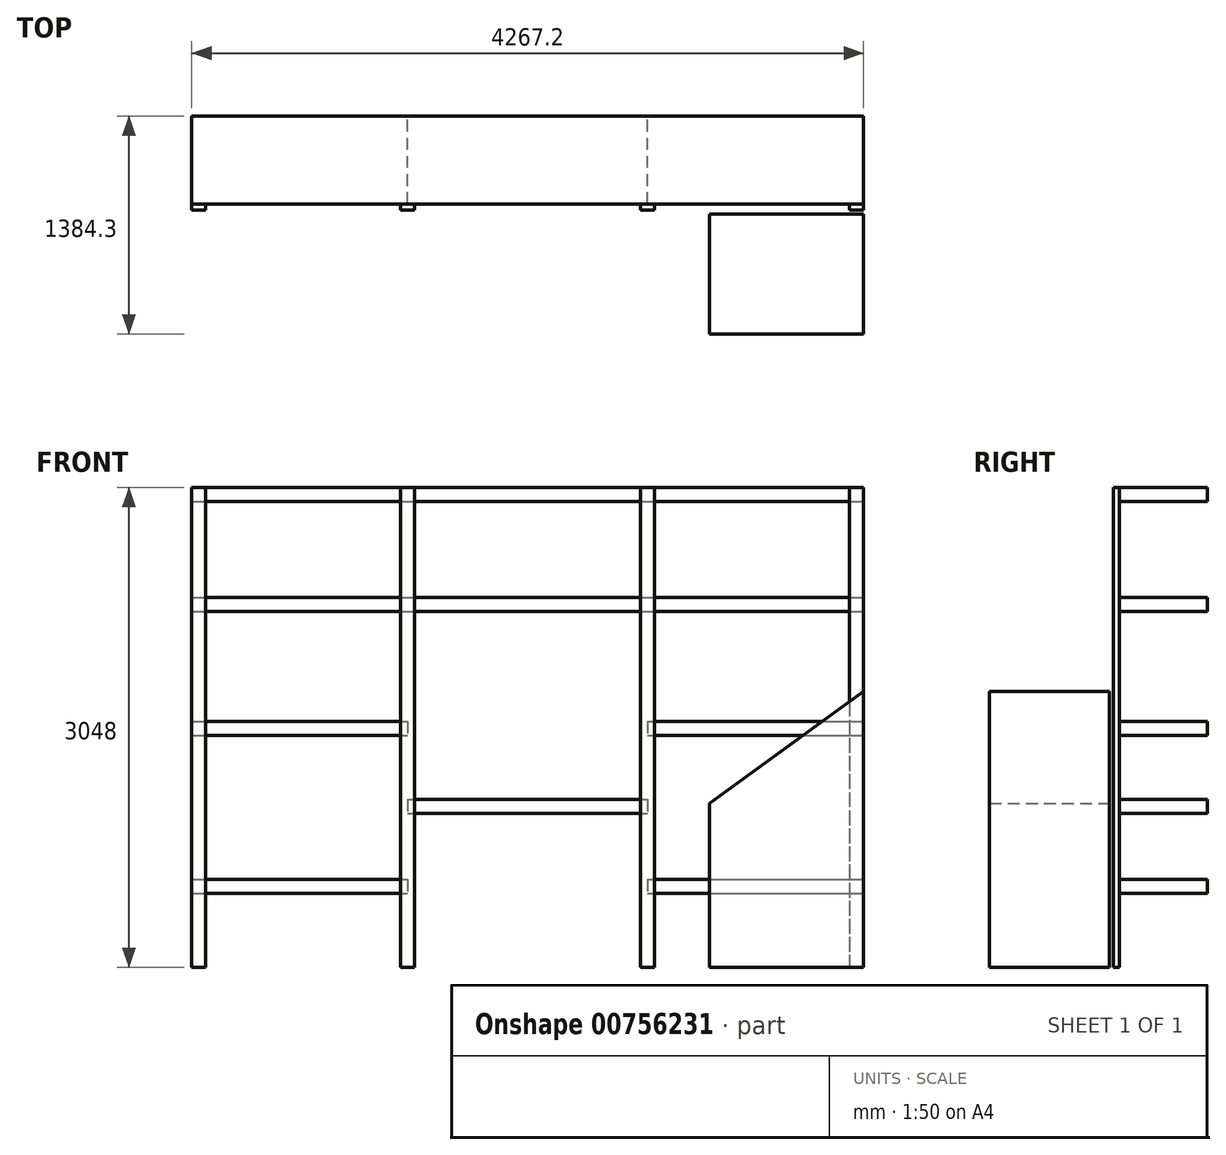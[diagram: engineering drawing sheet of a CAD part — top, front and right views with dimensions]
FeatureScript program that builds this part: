
annotation { "Feature Type Name" : "Feature", "Feature Type Description" : "" }
export const myFeature = defineFeature(function(context is Context, id is Id, definition is map)
    precondition{}
    {
        {
            var Q0;
            Q0=qCreatedBy(makeId("Top.planeOp"),FACE);
            var sketch = newSketch(context, id + "F0", { "sketchPlane" : qUnion([Q0])});
            skLineSegment(sketch, "E0", {"start": v(0, 0) * mm, "end": v(0, 8534.4) * mm});
            skLineSegment(sketch, "E1", {"start": v(0, 8534.4) * mm, "end": v(4267.2, 8534.4) * mm});
            skLineSegment(sketch, "E2", {"start": v(4267.2, 8534.4) * mm, "end": v(4267.2, 5791.2) * mm});
            skLineSegment(sketch, "E3", {"start": v(4267.2, 5791.2) * mm, "end": v(6705.6, 5791.2) * mm});
            skLineSegment(sketch, "E4", {"start": v(6705.6, 5791.2) * mm, "end": v(6705.6, 0) * mm});
            skLineSegment(sketch, "E5", {"start": v(6705.6, 0) * mm, "end": v(0, 0) * mm});
            skSolve(sketch);
        }
        {
            var Q0;
            Q0=sQuery(id+"F0.wireOp",EDGE,"E1");
            var Q1;
            Q1=sQuery(id+"F0.wireOp",EDGE,"E2");
            cPlane(context, id + "F1", {"entities" : qUnion([Q0, Q1]), "cplaneType" : CPlaneType.LINE_ANGLE, "offset" : 0 * mm, "angle" : 90 * degree, "width" : 152.4 * mm, "height" : 152.4 * mm});
        }
        {
            var Q0;
            Q0=qCreatedBy(id+"F1.planeOp",FACE);
            cPlane(context, id + "F2", {"entities" : qUnion([Q0]), "cplaneType" : CPlaneType.OFFSET, "offset" : 622.3 * mm, "oppositeDirection" : true, "width" : 152.4 * mm, "height" : 152.4 * mm});
        }
        {
            var Q0;
            Q0=qCreatedBy(id+"F2.planeOp",FACE);
            var sketch = newSketch(context, id + "F3", { "sketchPlane" : qUnion([Q0])});
            skLineSegment(sketch, "E6", {"start": v(-4267.2, 1752.6) * mm, "end": v(-4267.2, 0) * mm});
            skLineSegment(sketch, "E7", {"start": v(-3289.3, 0) * mm, "end": v(-4267.2, 0) * mm});
            skLineSegment(sketch, "E8", {"start": v(-3289.3, 0) * mm, "end": v(-3289.3, 1041.4) * mm});
            skLineSegment(sketch, "E9", {"start": v(-3289.3, 1041.4) * mm, "end": v(-4267.2, 1752.6) * mm});
            skSolve(sketch);
        }
        {
            var Q0;
            Q0 = qSketchRegion(id + "F3", true);
            extrude(context, id + "F4", {"entities" : qUnion([Q0]), "oppositeDirection" : true, "depth" : 762 * mm, "offsetDistance" : 25.4 * mm});
        }
        {
            var Q0;
            Q0=qCreatedBy(id+"F1.planeOp",FACE);
            var sketch = newSketch(context, id + "F5", { "sketchPlane" : qUnion([Q0])});
            skLineSegment(sketch, "E10.0", {"start": v(0, 0) * mm, "end": v(-4267.2, 0) * mm, "construction": true});
            skLineSegment(sketch, "E11.bottom", {"start": v(-1371.6, 1066.8) * mm, "end": v(-2895.6, 1066.8) * mm});
            skLineSegment(sketch, "E11.top", {"start": v(-1371.6, 977.9) * mm, "end": v(-2895.6, 977.9) * mm});
            skLineSegment(sketch, "E11.left", {"start": v(-1371.6, 1066.8) * mm, "end": v(-1371.6, 977.9) * mm});
            skLineSegment(sketch, "E11.right", {"start": v(-2895.6, 1066.8) * mm, "end": v(-2895.6, 977.9) * mm});
            skLineSegment(sketch, "E12", {"start": v(0, 3657.6) * mm, "end": v(-1371.6, 3657.6) * mm, "construction": true});
            skLineSegment(sketch, "E13", {"start": v(-2895.6, 3657.6) * mm, "end": v(-4267.2, 3657.6) * mm, "construction": true});
            skLineSegment(sketch, "E14", {"start": v(-1371.6, 3657.6) * mm, "end": v(-2895.6, 3657.6) * mm, "construction": true});
            skLineSegment(sketch, "E15.bottom", {"start": v(0, 1562.1) * mm, "end": v(-1371.6, 1562.1) * mm});
            skLineSegment(sketch, "E15.top", {"start": v(0, 1473.2) * mm, "end": v(-1371.6, 1473.2) * mm});
            skLineSegment(sketch, "E15.left", {"start": v(0, 1562.1) * mm, "end": v(0, 1473.2) * mm});
            skLineSegment(sketch, "E15.right", {"start": v(-1371.6, 1562.1) * mm, "end": v(-1371.6, 1473.2) * mm});
            skLineSegment(sketch, "E16.bottom", {"start": v(0, 558.8) * mm, "end": v(-1371.6, 558.8) * mm});
            skLineSegment(sketch, "E16.top", {"start": v(0, 469.9) * mm, "end": v(-1371.6, 469.9) * mm});
            skLineSegment(sketch, "E16.left", {"start": v(0, 558.8) * mm, "end": v(0, 469.9) * mm});
            skLineSegment(sketch, "E16.right", {"start": v(-1371.6, 558.8) * mm, "end": v(-1371.6, 469.9) * mm});
            skLineSegment(sketch, "E17.bottom", {"start": v(0, 3048) * mm, "end": v(-4267.2, 3048) * mm});
            skLineSegment(sketch, "E17.top", {"start": v(0, 2959.1) * mm, "end": v(-4267.2, 2959.1) * mm});
            skLineSegment(sketch, "E17.left", {"start": v(0, 3048) * mm, "end": v(0, 2959.1) * mm});
            skLineSegment(sketch, "E17.right", {"start": v(-4267.2, 3048) * mm, "end": v(-4267.2, 2959.1) * mm});
            skLineSegment(sketch, "E18.bottom", {"start": v(-2895.6, 1562.1) * mm, "end": v(-4267.2, 1562.1) * mm});
            skLineSegment(sketch, "E18.top", {"start": v(-2895.6, 1473.2) * mm, "end": v(-4267.2, 1473.2) * mm});
            skLineSegment(sketch, "E18.left", {"start": v(-2895.6, 1562.1) * mm, "end": v(-2895.6, 1473.2) * mm});
            skLineSegment(sketch, "E18.right", {"start": v(-4267.2, 1562.1) * mm, "end": v(-4267.2, 1473.2) * mm});
            skLineSegment(sketch, "E19.bottom", {"start": v(-2895.6, 558.8) * mm, "end": v(-4267.2, 558.8) * mm});
            skLineSegment(sketch, "E19.top", {"start": v(-2895.6, 469.9) * mm, "end": v(-4267.2, 469.9) * mm});
            skLineSegment(sketch, "E19.left", {"start": v(-2895.6, 558.8) * mm, "end": v(-2895.6, 469.9) * mm});
            skLineSegment(sketch, "E19.right", {"start": v(-4267.2, 558.8) * mm, "end": v(-4267.2, 469.9) * mm});
            skLineSegment(sketch, "E20", {"start": v(0, 3657.6) * mm, "end": v(0, 3048) * mm, "construction": true});
            skLineSegment(sketch, "E21", {"start": v(0, 2959.1) * mm, "end": v(0, 1562.1) * mm, "construction": true});
            skLineSegment(sketch, "E22", {"start": v(0, 1473.2) * mm, "end": v(0, 558.8) * mm, "construction": true});
            skLineSegment(sketch, "E23", {"start": v(0, 469.9) * mm, "end": v(0, 0) * mm, "construction": true});
            skLineSegment(sketch, "E24", {"start": v(-1371.6, 469.9) * mm, "end": v(-1371.6, 0) * mm, "construction": true});
            skLineSegment(sketch, "E25", {"start": v(-1371.6, 1473.2) * mm, "end": v(-1371.6, 1066.8) * mm, "construction": true});
            skLineSegment(sketch, "E26", {"start": v(-1371.6, 977.9) * mm, "end": v(-1371.6, 558.8) * mm, "construction": true});
            skLineSegment(sketch, "E27", {"start": v(-2895.6, 469.9) * mm, "end": v(-2895.6, 0) * mm, "construction": true});
            skLineSegment(sketch, "E28", {"start": v(-2895.6, 1473.2) * mm, "end": v(-2895.6, 1066.8) * mm, "construction": true});
            skLineSegment(sketch, "E29", {"start": v(-4267.2, 2959.1) * mm, "end": v(-4267.2, 1562.1) * mm, "construction": true});
            skLineSegment(sketch, "E30", {"start": v(-4267.2, 1473.2) * mm, "end": v(-4267.2, 558.8) * mm, "construction": true});
            skLineSegment(sketch, "E31", {"start": v(-4267.2, 469.9) * mm, "end": v(-4267.2, 0) * mm, "construction": true});
            skLineSegment(sketch, "E32", {"start": v(-4267.2, 3657.6) * mm, "end": v(-4267.2, 3048) * mm, "construction": true});
            skLineSegment(sketch, "E33", {"start": v(-2895.6, 977.9) * mm, "end": v(-2895.6, 558.8) * mm, "construction": true});
            skLineSegment(sketch, "E34.bottom", {"start": v(0, 2349.5) * mm, "end": v(-4267.2, 2349.5) * mm});
            skLineSegment(sketch, "E34.top", {"start": v(0, 2260.6) * mm, "end": v(-4267.2, 2260.6) * mm});
            skLineSegment(sketch, "E34.left", {"start": v(0, 2349.5) * mm, "end": v(0, 2260.6) * mm});
            skLineSegment(sketch, "E34.right", {"start": v(-4267.2, 2349.5) * mm, "end": v(-4267.2, 2260.6) * mm});
            skLineSegment(sketch, "E35", {"start": v(-1371.6, 1562.1) * mm, "end": v(-2895.6, 1562.1) * mm, "construction": true});
            skLineSegment(sketch, "E36", {"start": v(-1371.6, 1562.1) * mm, "end": v(-1371.6, 3657.6) * mm, "construction": true});
            skLineSegment(sketch, "E37", {"start": v(-2895.6, 3657.6) * mm, "end": v(-2895.6, 1562.1) * mm, "construction": true});
            skLineSegment(sketch, "E38", {"start": v(-1371.6, 558.8) * mm, "end": v(-2895.6, 558.8) * mm, "construction": true});
            skSolve(sketch);
        }
        {
            var Q0;
            Q0 = qSketchRegion(id + "F5", true);
            extrude(context, id + "F6", {"entities" : qUnion([Q0]), "oppositeDirection" : true, "depth" : 558.8 * mm, "offsetDistance" : 25.4 * mm});
        }
        {
            var Q0;
            Q0=makeQuery(id+"F0.imprint","IMPRINT",FACE,{"disambiguationData":[TD([[makeQuery(id+"F0.imprint","IMPRINT",EDGE,{"derivedFrom":sQuery(id+"F0.wireOp",EDGE,"E0")}),-1.0]])]});
            var sketch = newSketch(context, id + "F7", { "sketchPlane" : qUnion([Q0])});
            skPoint(sketch, "E39.0", {"position": v(0, 7975.6) * mm});
            skPoint(sketch, "E40.0", {"position": v(1371.6, 7975.6) * mm});
            skPoint(sketch, "E41.0", {"position": v(2895.6, 7975.6) * mm});
            skPoint(sketch, "E42.0", {"position": v(4267.2, 7975.6) * mm});
            skLineSegment(sketch, "E43.bottom", {"start": v(4267.2, 7975.6) * mm, "end": v(4178.3, 7975.6) * mm});
            skLineSegment(sketch, "E43.top", {"start": v(4267.2, 7937.5) * mm, "end": v(4178.3, 7937.5) * mm});
            skLineSegment(sketch, "E43.left", {"start": v(4267.2, 7975.6) * mm, "end": v(4267.2, 7937.5) * mm});
            skLineSegment(sketch, "E43.right", {"start": v(4178.3, 7975.6) * mm, "end": v(4178.3, 7937.5) * mm});
            skLineSegment(sketch, "E44.bottom", {"start": v(2851.15, 7975.6) * mm, "end": v(2940.05, 7975.6) * mm});
            skLineSegment(sketch, "E44.top", {"start": v(2851.15, 7937.5) * mm, "end": v(2940.05, 7937.5) * mm});
            skLineSegment(sketch, "E44.left", {"start": v(2851.15, 7975.6) * mm, "end": v(2851.15, 7937.5) * mm});
            skLineSegment(sketch, "E44.right", {"start": v(2940.05, 7975.6) * mm, "end": v(2940.05, 7937.5) * mm});
            skLineSegment(sketch, "E45.bottom", {"start": v(1327.15, 7975.6) * mm, "end": v(1416.05, 7975.6) * mm});
            skLineSegment(sketch, "E45.top", {"start": v(1327.15, 7937.5) * mm, "end": v(1416.05, 7937.5) * mm});
            skLineSegment(sketch, "E45.left", {"start": v(1327.15, 7975.6) * mm, "end": v(1327.15, 7937.5) * mm});
            skLineSegment(sketch, "E45.right", {"start": v(1416.05, 7975.6) * mm, "end": v(1416.05, 7937.5) * mm});
            skLineSegment(sketch, "E46.bottom", {"start": v(0, 7975.6) * mm, "end": v(88.9, 7975.6) * mm});
            skLineSegment(sketch, "E46.top", {"start": v(0, 7937.5) * mm, "end": v(88.9, 7937.5) * mm});
            skLineSegment(sketch, "E46.left", {"start": v(0, 7975.6) * mm, "end": v(0, 7937.5) * mm});
            skLineSegment(sketch, "E46.right", {"start": v(88.9, 7975.6) * mm, "end": v(88.9, 7937.5) * mm});
            skLineSegment(sketch, "E47", {"start": v(88.9, 7937.5) * mm, "end": v(1327.15, 7937.5) * mm, "construction": true});
            skLineSegment(sketch, "E48", {"start": v(1416.05, 7937.5) * mm, "end": v(2851.15, 7937.5) * mm, "construction": true});
            skLineSegment(sketch, "E49", {"start": v(2940.05, 7937.5) * mm, "end": v(4178.3, 7937.5) * mm, "construction": true});
            skSolve(sketch);
        }
        {
            var Q0;
            Q0 = qSketchRegion(id + "F7", true);
            extrude(context, id + "F8", {"entities" : qUnion([Q0]), "depth" : 3048 * mm, "offsetDistance" : 25.4 * mm});
        }
    });
